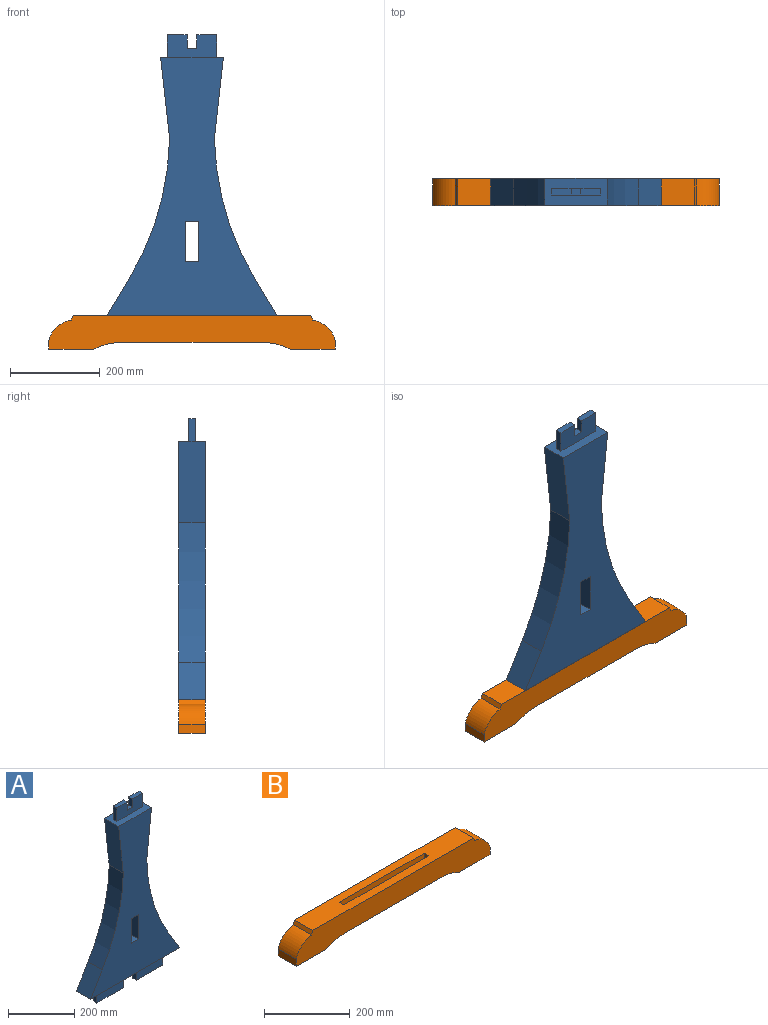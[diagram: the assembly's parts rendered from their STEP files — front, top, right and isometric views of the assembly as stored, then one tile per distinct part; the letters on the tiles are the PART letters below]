
ASSEMBLY  parts=2 mates=1
PART A: 32 faces, bbox 380x60x677 mm
  f0: plane 50x15mm, normal (-1,0,0), area 750mm2, adj f1,f16,f30,f31
  f1: plane 112x15mm, normal (0,0,-1), area 1680mm2, adj f0,f7,f30,f31
  f2: plane 112x15mm, normal (0,0,-1), area 1680mm2, adj f3,f9,f30,f31
  f3: plane 50x15mm, normal (1,0,0), area 750mm2, adj f2,f16,f30,f31
  f4: plane 50x15mm, normal (1,0,0), area 750mm2, adj f5,f20,f28,f29
  f5: plane 44x15mm, normal (0,0,1), area 660mm2, adj f4,f10,f28,f29
  f6: plane 44x15mm, normal (0,0,1), area 660mm2, adj f12,f13,f28,f29
  f7: plane 30x15mm, normal (1,0,0), area 450mm2, adj f1,f8,f30,f31
  f8: plane 56x15mm, normal (0,0,-1), area 840mm2, adj f7,f9,f30,f31
  f9: plane 30x15mm, normal (-1,0,0), area 450mm2, adj f2,f8,f30,f31
  f10: plane 30x15mm, normal (-1,0,0), area 450mm2, adj f5,f11,f28,f29
  f11: plane 22x15mm, normal (0,0,1), area 330mm2, adj f10,f12,f28,f29
  f12: plane 30x15mm, normal (1,0,0), area 450mm2, adj f6,f11,f28,f29
  f13: plane 50x15mm, normal (-1,0,0), area 750mm2, adj f6,f20,f28,f29
  f14: plane 577x380mm, normal (0,1,0), area 96595.1mm2, adj f16,f17,f18,f19,f20,f21,f22,f23
  f15: plane 577x380mm, normal (0,-1,0), area 96595.1mm2, adj f16,f17,f18,f19,f20,f21,f22,f23
  f16: plane 380x60mm, normal (0,0,-1), area 18600mm2, adj f0,f3,f14,f15,f17,f27,f30,f31
  f17: plane 83x60mm, normal (0.86,0,0.52), area 5813.8mm2, adj f14,f15,f16,f18
  f18: cylinder r=632mm len=312mm, axis (0,-1,0), area 19704.2mm2, adj f14,f15,f17,f19
  f19: plane 182x60mm, normal (0.99,0,-0.11), area 10985.7mm2, adj f14,f15,f18,f20
  f20: plane 140x60mm, normal (0,0,1), area 6750mm2, adj f4,f13,f14,f15,f19,f21,f28,f29
  f21: plane 182x60mm, normal (-0.99,0,-0.11), area 10985.7mm2, adj f14,f15,f20,f22
  f22: cylinder r=632mm len=312mm, axis (0,-1,0), area 19704.2mm2, adj f14,f15,f21,f27
  f23: plane 90x60mm, normal (1,0,0), area 5400mm2, adj f14,f15,f24,f26
  f24: plane 60x30mm, normal (0,0,-1), area 1800mm2, adj f14,f15,f23,f25
  f25: plane 90x60mm, normal (-1,0,0), area 5400mm2, adj f14,f15,f24,f26
  f26: plane 60x30mm, normal (0,0,1), area 1800mm2, adj f14,f15,f23,f25
  f27: plane 83x60mm, normal (-0.86,0,0.52), area 5813.8mm2, adj f14,f15,f16,f22
  f28: plane 110x50mm, normal (0,1,0), area 4840mm2, adj f4,f5,f6,f10,f11,f12,f13,f20
  f29: plane 110x50mm, normal (0,-1,0), area 4840mm2, adj f4,f5,f6,f10,f11,f12,f13,f20
  f30: plane 280x50mm, normal (0,-1,0), area 12320mm2, adj f0,f1,f2,f3,f7,f8,f9,f16
  f31: plane 280x50mm, normal (0,1,0), area 12320mm2, adj f0,f1,f2,f3,f7,f8,f9,f16
PART B: 25 faces, bbox 640x60x75 mm
  f0: plane 529.37x60mm, normal (0,0,1), area 27561.9mm2, adj f4,f5,f10,f11,f17,f19,f20,f21
  f1: plane 100x60mm, normal (0,0,-1), area 6000mm2, adj f2,f10,f11,f13
  f2: plane 60x20mm, normal (1,0,0), area 1200mm2, adj f1,f3,f10,f11
  f3: cylinder r=63mm len=60mm, axis (0,-1,0), area 4257.6mm2, adj f2,f4,f10,f11
  f4: plane 60x10mm, normal (0.88,0,0.47), area 679.5mm2, adj f0,f3,f10,f11
  f5: plane 60x10mm, normal (-0.88,0,0.47), area 679.5mm2, adj f0,f6,f10,f11
  f6: cylinder r=63mm len=60mm, axis (0,-1,0), area 4257.6mm2, adj f5,f7,f10,f11
  f7: plane 60x20mm, normal (-1,0,0), area 1200mm2, adj f6,f8,f10,f11
  f8: plane 100x60mm, normal (0,0,-1), area 6000mm2, adj f7,f10,f11,f12
  f9: plane 313.9x60mm, normal (0,0,-1), area 18834.1mm2, adj f10,f11,f14,f15
  f10: plane 640x75mm, normal (0,1,0), area 39600.3mm2, adj f0,f1,f2,f3,f4,f5,f6,f7
  f11: plane 640x75mm, normal (0,-1,0), area 39600.3mm2, adj f0,f1,f2,f3,f4,f5,f6,f7
  f12: plane 60x0.44mm, normal (0.45,0,-0.89), area 29.5mm2, adj f8,f10,f11,f14
  f13: plane 60x0.44mm, normal (-0.45,0,-0.89), area 29.5mm2, adj f1,f10,f11,f15
  f14: cylinder r=140mm len=62.61mm, axis (0,-1,0), area 3894.6mm2, adj f9,f10,f11,f12
  f15: cylinder r=140mm len=62.61mm, axis (0,-1,0), area 3894.6mm2, adj f9,f10,f11,f13
  f16: plane 30x15mm, normal (1,0,0), area 450mm2, adj f18,f19,f21,f24
  f17: plane 50x15mm, normal (-1,0,0), area 750mm2, adj f0,f18,f19,f21
  f18: plane 112x15mm, normal (0,0,1), area 1680mm2, adj f16,f17,f19,f21
  f19: plane 280x50mm, normal (0,-1,0), area 12320mm2, adj f0,f16,f17,f18,f20,f22,f23,f24
  f20: plane 50x15mm, normal (1,0,0), area 750mm2, adj f0,f19,f21,f23
  f21: plane 280x50mm, normal (0,1,0), area 12320mm2, adj f0,f16,f17,f18,f20,f22,f23,f24
  f22: plane 30x15mm, normal (-1,0,0), area 450mm2, adj f19,f21,f23,f24
  f23: plane 112x15mm, normal (0,0,1), area 1680mm2, adj f19,f20,f21,f22
  f24: plane 56x15mm, normal (0,0,1), area 840mm2, adj f16,f19,f21,f22
PLACE A t=(26.78,-21.85,262.49)mm
PLACE B t=(-155.38,-21.85,-72.47)mm
MATE fastened A.f8 <-> B.f24  axis (0,0,-1) through (23.07,8.15,-42.19)mm
